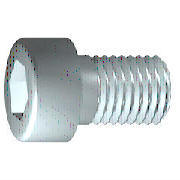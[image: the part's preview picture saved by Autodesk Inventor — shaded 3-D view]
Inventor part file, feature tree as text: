
AUTODESK INVENTOR PART (.ipt)
format: ipt  version: 2024.2 (Build 282272000, 272)  size: 193,536 bytes
history: native  units: mm (DEFAULTED — no unit token found)
features: extrude x1, plane x1, fillet x1
ambient origin geometry x7: Origin, YZ Plane, XY Plane, X Axis, Y Axis, Z Axis, Center Point
bodies: Solid1 (feature_tree), Body (feature_tree)
feature tree (3):
  extrude  "Slot"  Depth=8.25mm
  plane  "Work Plane1"
  fillet  "Fillet2"  Radius=0.429515mm
